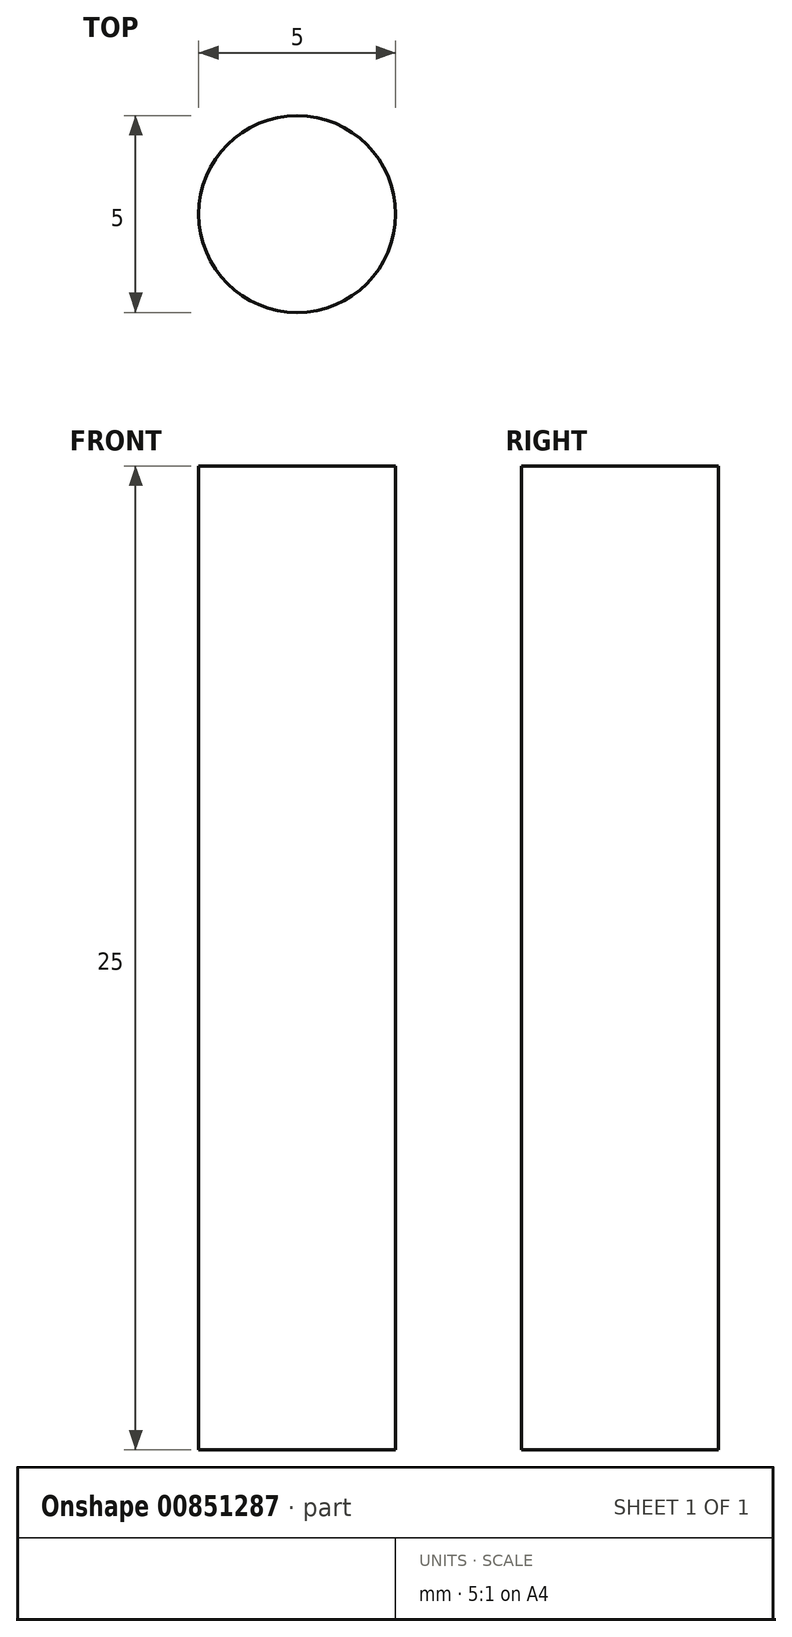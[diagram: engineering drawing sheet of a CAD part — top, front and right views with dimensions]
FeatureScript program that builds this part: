
annotation { "Feature Type Name" : "Feature", "Feature Type Description" : "" }
export const myFeature = defineFeature(function(context is Context, id is Id, definition is map)
    precondition{}
    {
        {
            var Q0;
            Q0=qCreatedBy(makeId("Top.planeOp"),FACE);
            var sketch = newSketch(context, id + "F0", { "sketchPlane" : qUnion([Q0])});
            skCircle(sketch, "E0", {"center": v(0, 0) * mm, "radius": 2.5 * mm});
            skSolve(sketch);
        }
        {
            var Q0;
            Q0=makeQuery(id+"F0.imprint","IMPRINT",FACE,{"disambiguationData":[TD([[makeQuery(id+"F0.imprint","IMPRINT",EDGE,{"derivedFrom":sQuery(id+"F0.wireOp",EDGE,"E0")}),1.0]])]});
            extrude(context, id + "F1", {"entities" : qUnion([Q0]), "depth" : 25 * mm, "offsetDistance" : 25 * mm});
        }
    });
